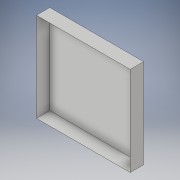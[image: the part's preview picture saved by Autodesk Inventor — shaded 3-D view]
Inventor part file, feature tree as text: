
AUTODESK INVENTOR PART (.ipt)
format: ipt  version: 2017 (Build 210142000, 142)  size: 93,184 bytes
history: native  units: in
note: dims shown in document units (in); Inventor stores cm internally (conversion verified against a paired STEP export)
features: extrude x1, other x1, sketch x1
ambient origin geometry x8: Origin, YZ Plane, XZ Plane, XY Plane, X Axis, Y Axis, Z Axis, Center Point
bodies: Solid1 (feature_tree)
feature tree (3):
  extrude  "end cap"  Depth=6.6667in
  other  "removed end"
  sketch  "Sketch1"  dims[d0=7.0in d1=6.6667in d2=1.0in d3=0.0in]
